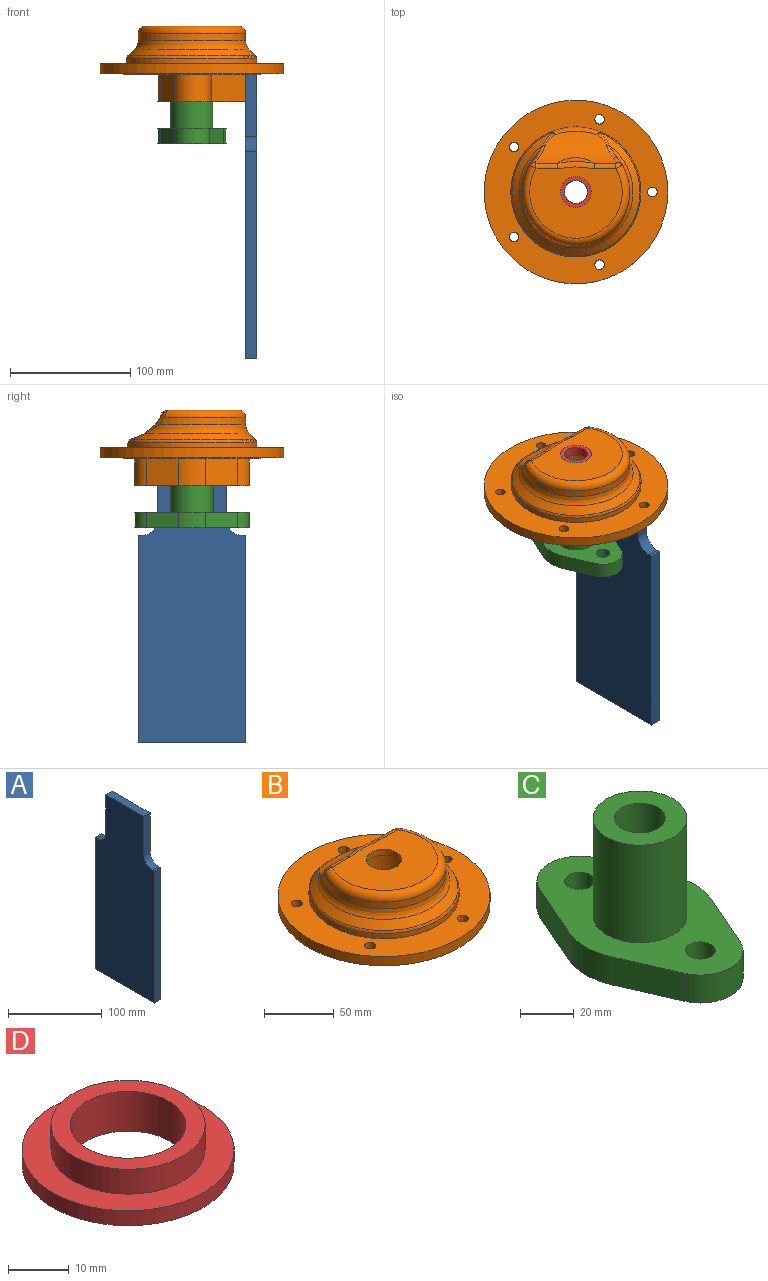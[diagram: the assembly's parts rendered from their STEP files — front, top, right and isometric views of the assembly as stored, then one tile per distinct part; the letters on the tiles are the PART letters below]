
ASSEMBLY  parts=4 mates=3
PART A: 12 faces, bbox 9.5x88.9x235 mm
  f0: plane 57.15x9.53mm, normal (0,0,1), area 544.4mm2, adj f1,f9,f10,f11
  f1: plane 50.8x9.53mm, normal (0,-1,0), area 483.9mm2, adj f0,f2,f10,f11
  f2: cylinder r=12.7mm len=12.7mm, axis (-1,0,0), area 190mm2, adj f1,f3,f10,f11
  f3: plane 9.53x3.18mm, normal (0,0,1), area 30.2mm2, adj f2,f4,f10,f11
  f4: plane 171.45x9.53mm, normal (0,-1,0), area 1633.1mm2, adj f3,f5,f10,f11
  f5: plane 88.9x9.53mm, normal (0,0,-1), area 846.8mm2, adj f4,f6,f10,f11
  f6: plane 171.45x9.53mm, normal (0,1,0), area 1633.1mm2, adj f5,f7,f10,f11
  f7: plane 9.53x3.18mm, normal (0,0,1), area 30.2mm2, adj f6,f8,f10,f11
  f8: cylinder r=12.7mm len=12.7mm, axis (-1,0,0), area 190mm2, adj f7,f9,f10,f11
  f9: plane 50.8x9.53mm, normal (0,1,0), area 483.9mm2, adj f0,f8,f10,f11
  f10: plane 234.95x88.9mm, normal (1,0,0), area 18940.2mm2, adj f0,f1,f2,f3,f4,f5,f6,f7
  f11: plane 234.95x88.9mm, normal (-1,0,0), area 18940.2mm2, adj f0,f1,f2,f3,f4,f5,f6,f7
PART B: 60 faces, bbox 152.4x152.4x69.9 mm
  f0: plane 114.3x113.9mm, normal (0,0,-1), area 5156.4mm2, adj f1,f2,f3,f4,f5,f19,f20,f21
  f1: cylinder r=57.15mm len=53.11mm, axis (0,0,1), area 58.3mm2, adj f0,f16,f38,f41
  f2: cylinder r=57.15mm len=45.17mm, axis (0,0,1), area 58.3mm2, adj f0,f16,f37,f40
  f3: cylinder r=57.15mm len=53.11mm, axis (0,0,1), area 58.3mm2, adj f0,f16,f39,f40
  f4: cylinder r=57.15mm len=55.84mm, axis (0,0,1), area 58.3mm2, adj f0,f16,f38,f39
  f5: cylinder r=57.15mm len=45.17mm, axis (0,0,1), area 58.3mm2, adj f0,f16,f37,f41
  f6: cylinder r=12.7mm len=25.4mm, axis (0,0,1), area 399mm2, adj f7,f18
  f7: plane 76.9x59.2mm, normal (0,0,1), area 3267.5mm2, adj f6,f8,f52,f54,f56
  f8: torus R=38.45mm, axis (0,0,1), area 1672.5mm2, adj f7,f9,f49,f58
  f9: cylinder r=44.45mm len=88.9mm, axis (0,0,1), area 1173.6mm2, adj f8,f10,f46,f59
  f10: torus R=54.45mm, axis (0,0,1), area 1698.1mm2, adj f9,f11,f44,f57
  f11: cone r=53.1mm half-angle=45deg, axis (0,0,-1), area 2160.2mm2, adj f10,f12,f45,f47,f50,f55
  f12: torus R=50.98mm, axis (0,0,1), area 675.7mm2, adj f11,f13,f47,f50
  f13: cylinder r=53.98mm len=107.95mm, axis (0,0,1), area 1526.1mm2, adj f12,f14,f51
  f14: plane 152.4x152.4mm, normal (0,0,1), area 8837.7mm2, adj f13,f15,f32,f33,f34,f35,f36
  f15: cylinder r=76.2mm len=152.4mm, axis (0,0,1), area 3878.1mm2, adj f14,f16
  f16: plane 152.4x152.4mm, normal (0,0,-1), area 7875.8mm2, adj f1,f2,f3,f4,f5,f15,f32,f33
  f17: cylinder r=17.46mm len=57.83mm, axis (0,0,1), area 6344.6mm2, adj f18,f29
  f18: plane 34.93x34.93mm, normal (0,0,-1), area 451.3mm2, adj f6,f17
  f19: plane 26.67x22.23mm, normal (-0.92,-0.4,0), area 646.7mm2, adj f0,f20,f28,f29
  f20: cylinder r=15.88mm len=30.42mm, axis (0,0,1), area 1034.3mm2, adj f0,f19,f21,f29
  f21: plane 28.9x22.23mm, normal (0,-1,0), area 642.2mm2, adj f0,f20,f22,f29
  f22: plane 57.15x22.23mm, normal (1,0,0), area 1270.2mm2, adj f0,f21,f23,f29
  f23: plane 28.9x22.23mm, normal (0,1,0), area 642.2mm2, adj f0,f22,f24,f29
  f24: cylinder r=15.88mm len=30.42mm, axis (0,0,1), area 1034.3mm2, adj f0,f23,f25,f29
  f25: plane 26.67x22.23mm, normal (-0.92,0.4,0), area 646.7mm2, adj f0,f24,f28,f29
  f26: cylinder r=5.56mm len=22.23mm, axis (0,0,1), area 775.9mm2, adj f29,f31
  f27: cylinder r=5.56mm len=22.23mm, axis (0,0,1), area 775.9mm2, adj f29,f30
  f28: cylinder r=28.57mm len=22.86mm, axis (0,0,1), area 522.7mm2, adj f0,f19,f25,f29
  f29: plane 95.25x73.03mm, normal (0,0,-1), area 3806mm2, adj f17,f19,f20,f21,f22,f23,f24,f25
  f30: plane 11.11x11.11mm, normal (0,0,-1), area 97mm2, adj f27
  f31: plane 11.11x11.11mm, normal (0,0,-1), area 97mm2, adj f26
  f32: cylinder r=4mm len=8.1mm, axis (0,0,-1), area 203.6mm2, adj f14,f16
  f33: cylinder r=4mm len=8.1mm, axis (0,0,-1), area 203.6mm2, adj f14,f16
  f34: cylinder r=4mm len=8.1mm, axis (0,0,-1), area 203.6mm2, adj f14,f16
  f35: cylinder r=4mm len=8.1mm, axis (0,0,-1), area 203.6mm2, adj f14,f16
  f36: cylinder r=4mm len=8.1mm, axis (0,0,-1), area 203.6mm2, adj f14,f16
  f37: cylinder r=9.53mm len=13.45mm, axis (0,0,1), area 14.9mm2, adj f0,f2,f5,f16
  f38: cylinder r=9.53mm len=10.88mm, axis (0,0,1), area 14.9mm2, adj f0,f1,f4,f16
  f39: cylinder r=9.53mm len=10.88mm, axis (0,0,1), area 14.9mm2, adj f0,f3,f4,f16
  f40: cylinder r=9.53mm len=12.79mm, axis (0,0,1), area 14.9mm2, adj f0,f2,f3,f16
  f41: cylinder r=9.53mm len=12.79mm, axis (0,0,1), area 14.9mm2, adj f0,f1,f5,f16
  f42: cylinder r=45.14mm len=67.94mm, axis (-1,0,0), area 1660mm2, adj f43,f44,f45,f46,f49,f51,f52,f55
  f43: bspline ~34.5x16.45mm, area 0mm2, adj f42,f54
  f44: bspline ~14.82x13.42mm, area 56.4mm2, adj f10,f42,f45,f46
  f45: bspline ~12.76x10.85mm, area 30.5mm2, adj f11,f42,f44,f48
  f46: bspline ~14.96x10.93mm, area 42.2mm2, adj f9,f42,f44,f49
  f47: bspline ~8.63x3.62mm, area 8.9mm2, adj f11,f12,f48,f51
  f48: bspline ~2.29x2.08mm, area 0.2mm2, adj f45,f47,f51
  f49: bspline ~6.41x5.95mm, area 26.4mm2, adj f8,f42,f46,f52
  f50: bspline ~7.29x3.04mm, area 8.9mm2, adj f11,f12,f51,f53
  f51: bspline ~55.8x10.82mm, area 262mm2, adj f13,f42,f47,f48,f50,f53
  f52: cylinder r=5mm len=17.8mm, axis (-1,0,0), area 95.3mm2, adj f7,f42,f49,f54
  f53: bspline ~2.29x2.07mm, area 0.2mm2, adj f50,f51,f55
  f54: bspline ~38.3x6.09mm, area 188.4mm2, adj f7,f43,f52,f56
  f55: bspline ~13.29x11.68mm, area 30.5mm2, adj f11,f42,f53,f57
  f56: cylinder r=5mm len=17.8mm, axis (-1,0,0), area 95.3mm2, adj f7,f42,f54,f58
  f57: bspline ~13.43x11.91mm, area 56.4mm2, adj f10,f42,f55,f59
  f58: bspline ~6.41x5.94mm, area 26.4mm2, adj f8,f42,f56,f59
  f59: bspline ~14.96x10.93mm, area 42.2mm2, adj f9,f42,f57,f58
PART C: 15 faces, bbox 57.2x95.3x57.2 mm
  f0: cylinder r=9.53mm len=57.15mm, axis (0,0,-1), area 3420.3mm2, adj f2,f13
  f1: cylinder r=17.46mm len=44.45mm, axis (0,0,-1), area 4877.1mm2, adj f2,f14
  f2: plane 34.93x34.93mm, normal (0,0,1), area 673mm2, adj f0,f1
  f3: cylinder r=28.57mm len=22.86mm, axis (0,0,1), area 298.7mm2, adj f4,f12,f13,f14
  f4: plane 26.67x12.7mm, normal (0.92,-0.4,0), area 369.6mm2, adj f3,f5,f13,f14
  f5: cylinder r=15.88mm len=29.1mm, axis (0,0,1), area 467.5mm2, adj f4,f6,f13,f14
  f6: plane 26.67x12.7mm, normal (-0.92,-0.4,0), area 369.6mm2, adj f5,f7,f13,f14
  f7: cylinder r=28.57mm len=22.86mm, axis (0,0,1), area 298.7mm2, adj f6,f8,f13,f14
  f8: plane 26.67x12.7mm, normal (-0.92,0.4,0), area 369.6mm2, adj f7,f9,f13,f14
  f9: cylinder r=15.88mm len=29.1mm, axis (0,0,1), area 467.5mm2, adj f8,f12,f13,f14
  f10: cylinder r=5.56mm len=12.7mm, axis (0,0,1), area 443.4mm2, adj f13,f14
  f11: cylinder r=5.56mm len=12.7mm, axis (0,0,1), area 443.4mm2, adj f13,f14
  f12: plane 26.67x12.7mm, normal (0.92,0.4,0), area 369.6mm2, adj f3,f9,f13,f14
  f13: plane 95.25x57.15mm, normal (0,0,-1), area 3364.3mm2, adj f0,f3,f4,f5,f6,f7,f8,f9
  f14: plane 95.25x57.15mm, normal (0,0,1), area 2691.3mm2, adj f1,f3,f4,f5,f6,f7,f8,f9
PART D: 6 faces, bbox 34.9x34.9x8 mm
  f0: cylinder r=17.46mm len=34.93mm, axis (0,0,1), area 329.2mm2, adj f1,f5
  f1: plane 34.93x34.93mm, normal (0,0,-1), area 673mm2, adj f0,f2
  f2: cylinder r=9.53mm len=19.05mm, axis (0,0,1), area 478.8mm2, adj f1,f3
  f3: plane 25.4x25.4mm, normal (0,0,1), area 221.7mm2, adj f2,f4
  f4: cylinder r=12.7mm len=25.4mm, axis (0,0,1), area 399mm2, adj f3,f5
  f5: plane 34.93x34.93mm, normal (0,0,1), area 451.3mm2, adj f0,f4
PLACE A t=(0,152.4,0)mm
PLACE B at identity
PLACE C t=(0,152.4,-3.17)mm
PLACE D t=(0,304.8,0)mm
MATE fastened D.f0 <-> B.f1  axis (0,0,1) through (0,152.4,26.5)mm
MATE fastened A.f11 <-> B.f22  axis (-1,0,0) through (44.45,152.4,-9.1)mm
MATE fastened C.f1 <-> B.f1  axis (0,0,-1) through (0,152.4,-31.32)mm
